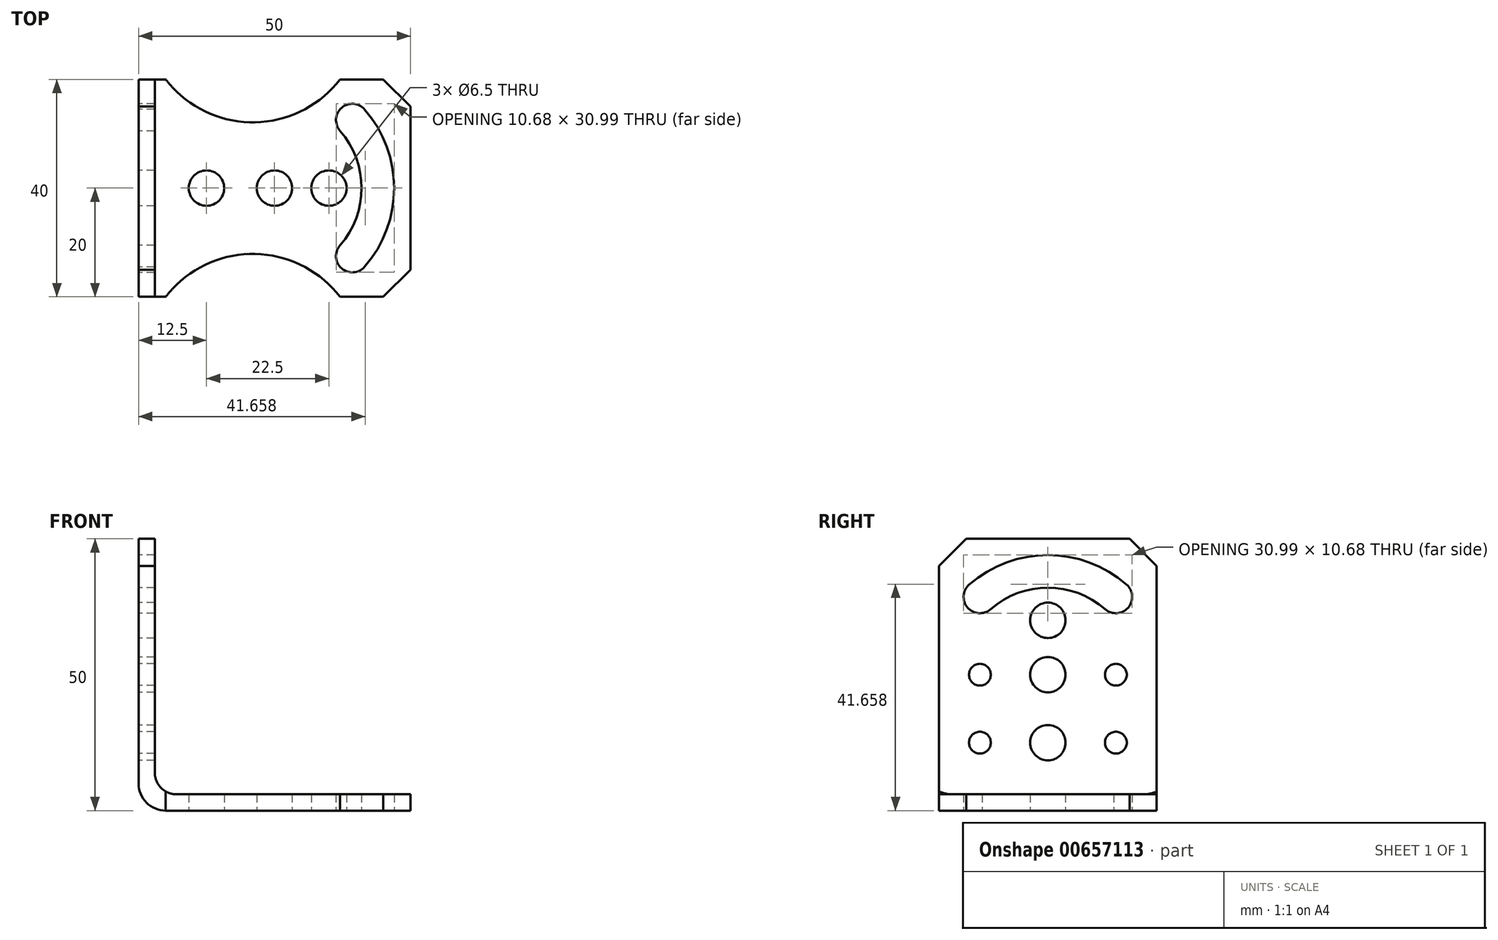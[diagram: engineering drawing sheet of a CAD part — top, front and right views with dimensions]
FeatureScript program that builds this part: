
annotation { "Feature Type Name" : "Feature", "Feature Type Description" : "" }
export const myFeature = defineFeature(function(context is Context, id is Id, definition is map)
    precondition{}
    {
        {
            var Q0;
            Q0=qCreatedBy(makeId("Front.planeOp"),FACE);
            var sketch = newSketch(context, id + "F0", { "sketchPlane" : qUnion([Q0])});
            skLineSegment(sketch, "E0", {"start": v(0, 0) * mm, "end": v(50, 0) * mm});
            skLineSegment(sketch, "E1", {"start": v(50, 0) * mm, "end": v(50, 5) * mm});
            skLineSegment(sketch, "E2", {"start": v(50, 5) * mm, "end": v(5, 5) * mm});
            skLineSegment(sketch, "E3", {"start": v(5, 5) * mm, "end": v(5, 50) * mm});
            skLineSegment(sketch, "E4", {"start": v(5, 50) * mm, "end": v(0, 50) * mm});
            skLineSegment(sketch, "E5", {"start": v(0, 50) * mm, "end": v(0, 0) * mm});
            skSolve(sketch);
        }
        {
            var Q0;
            Q0=qSketchRegion(id+"F0",true);
            extrude(context, id + "F1", {"entities" : qUnion([Q0]), "depth" : 40 * mm, "offsetDistance" : 25 * mm});
        }
        {
            var Q0;
            Q0=makeQuery(id+"F1.opExtrude","SWEPT_FACE",FACE,{"disambiguationData":[OSD([sQuery(id+"F0.wireOp",EDGE,"E0")])]});
            var sketch = newSketch(context, id + "F2", { "sketchPlane" : qUnion([Q0])});
            skCircle(sketch, "E6", {"center": v(25, 20) * mm, "radius": 3.25 * mm});
            skPoint(sketch, "E6.centerSnap0", {"position": v(0, 20) * mm});
            skArc(sketch, "E7", {"start": v(37.05, 9.47) * mm, "mid": v(37.34, 5.24) * mm, "end": v(41.57, 5.53) * mm});
            skArc(sketch, "E8", {"start": v(41.57, 34.47) * mm, "mid": v(37.34, 34.76) * mm, "end": v(37.05, 30.53) * mm});
            skArc(sketch, "E9", {"start": v(37.05, 9.47) * mm, "mid": v(41, 20) * mm, "end": v(37.05, 30.53) * mm});
            skArc(sketch, "E10", {"start": v(41.57, 5.53) * mm, "mid": v(47, 20) * mm, "end": v(41.57, 34.47) * mm});
            skCircle(sketch, "E11", {"center": v(12.5, 20) * mm, "radius": 3.25 * mm});
            skCircle(sketch, "E12", {"center": v(35, 20) * mm, "radius": 3.25 * mm});
            skPoint(sketch, "E12.centerSnap0", {"position": v(41, 20) * mm});
            skArc(sketch, "E13", {"start": v(37.05, 0) * mm, "mid": v(21.02, 7.9) * mm, "end": v(5, 0) * mm});
            skArc(sketch, "E14", {"start": v(5, 40) * mm, "mid": v(21.02, 32.1) * mm, "end": v(37.05, 40) * mm});
            skLineSegment(sketch, "E15", {"start": v(37.05, 0) * mm, "end": v(26.55, -9.52) * mm});
            skLineSegment(sketch, "E16", {"start": v(26.55, -9.52) * mm, "end": v(5, 0) * mm});
            skLineSegment(sketch, "E17", {"start": v(5, 40) * mm, "end": v(21.02, 52.32) * mm});
            skLineSegment(sketch, "E18", {"start": v(37.05, 40) * mm, "end": v(21.02, 52.32) * mm});
            skSolve(sketch);
        }
        {
            var Q0;
            Q0=qSketchRegion(id+"F2",true);
            extrude(context, id + "F3", {"entities" : qUnion([Q0]), "operationType" : NewBodyOperationType.REMOVE, "oppositeDirection" : true, "depth" : 25 * mm, "offsetDistance" : 25 * mm});
        }
        {
            var Q0;
            Q0=makeQuery(id+"F1.opExtrude","SWEPT_FACE",FACE,{"disambiguationData":[OSD([sQuery(id+"F0.wireOp",EDGE,"E5")])]});
            var sketch = newSketch(context, id + "F4", { "sketchPlane" : qUnion([Q0])});
            skCircle(sketch, "E19", {"center": v(20, 12.5) * mm, "radius": 3.25 * mm});
            skPoint(sketch, "E19.centerSnap0", {"position": v(20, 0) * mm});
            skCircle(sketch, "E20", {"center": v(20, 25) * mm, "radius": 3.25 * mm});
            skCircle(sketch, "E21", {"center": v(20, 35) * mm, "radius": 3.25 * mm});
            skArc(sketch, "E22", {"start": v(30.53, 37.05) * mm, "mid": v(20, 41) * mm, "end": v(9.47, 37.05) * mm});
            skArc(sketch, "E23", {"start": v(5.53, 41.57) * mm, "mid": v(5.24, 37.34) * mm, "end": v(9.47, 37.05) * mm});
            skArc(sketch, "E24", {"start": v(30.53, 37.05) * mm, "mid": v(34.76, 37.34) * mm, "end": v(34.47, 41.57) * mm});
            skArc(sketch, "E25", {"start": v(34.47, 41.57) * mm, "mid": v(20, 47) * mm, "end": v(5.53, 41.57) * mm});
            skCircle(sketch, "E26", {"center": v(32.5, 12.5) * mm, "radius": 2 * mm});
            skCircle(sketch, "E27", {"center": v(32.5, 25) * mm, "radius": 2 * mm});
            skCircle(sketch, "E28", {"center": v(7.5, 25) * mm, "radius": 2 * mm});
            skCircle(sketch, "E29", {"center": v(7.5, 12.5) * mm, "radius": 2 * mm});
            skSolve(sketch);
        }
        {
            var Q0;
            Q0=qSketchRegion(id+"F4",true);
            extrude(context, id + "F5", {"entities" : qUnion([Q0]), "operationType" : NewBodyOperationType.REMOVE, "oppositeDirection" : true, "depth" : 25 * mm, "offsetDistance" : 25 * mm});
        }
        {
            var Q0;
            Q0=makeQuery(id+"F1.opExtrude","CAP_EDGE",EDGE,{"disambiguationData":[OSD([sQuery(id+"F0.wireOp",EDGE,"E1")])],"isStart":false});
            chamfer(context, id + "F6", {"entities" : qUnion([Q0]), "width" : 5 * mm, "tangentPropagation" : true});
        }
        {
            var Q0;
            Q0=makeQuery(id+"F1.opExtrude","CAP_EDGE",EDGE,{"disambiguationData":[OSD([sQuery(id+"F0.wireOp",EDGE,"E1")])],"isStart":true});
            chamfer(context, id + "F7", {"entities" : qUnion([Q0]), "width" : 5 * mm, "tangentPropagation" : true});
        }
        {
            var Q0;
            Q0=qSketchRegion(id+"F2",true);
            extrude(context, id + "F8", {"entities" : qUnion([Q0]), "operationType" : NewBodyOperationType.REMOVE, "depth" : 25 * mm, "offsetDistance" : 25 * mm});
        }
        {
            var Q0;
            {var subQ0=sQuery(id+"F0.wireOp",EDGE,"E4");var subQ1=sQuery(id+"F0.wireOp",EDGE,"E2");var subQ2=sQuery(id+"F0.wireOp",EDGE,"E3");var subQ3=sQuery(id+"F0.wireOp",EDGE,"E0");var subQ4=sQuery(id+"F0.wireOp",EDGE,"E5");Q0=makeQuery(id+"F3.boolean.opBoolean","SPLIT",FACE,{"disambiguationData":[TD([makeQuery(id+"F1.opExtrude","SWEPT_FACE",FACE,{"disambiguationData":[OSD([subQ2])]})])],"derivedFrom":makeQuery(id+"F1.opExtrude","CAP_FACE",FACE,{"disambiguationData":[OSD([subQ3,sQuery(id+"F0.wireOp",EDGE,"E1"),subQ1,subQ2,subQ0,subQ4])],"isStart":false})});}
            var sketch = newSketch(context, id + "F9", { "sketchPlane" : qUnion([Q0])});
            skLineSegment(sketch, "E30.bottom", {"start": v(3, 3) * mm, "end": v(53.79, 3) * mm});
            skLineSegment(sketch, "E30.top", {"start": v(3, 60.6) * mm, "end": v(53.79, 60.6) * mm});
            skLineSegment(sketch, "E30.left", {"start": v(3, 3) * mm, "end": v(3, 60.6) * mm});
            skLineSegment(sketch, "E30.right", {"start": v(53.79, 3) * mm, "end": v(53.79, 60.6) * mm});
            skSolve(sketch);
        }
        {
            var Q0;
            Q0=qSketchRegion(id+"F9",true);
            extrude(context, id + "F10", {"entities" : qUnion([Q0]), "operationType" : NewBodyOperationType.REMOVE, "oppositeDirection" : true, "depth" : 51.1 * mm, "offsetDistance" : 25 * mm});
        }
        {
            var Q0;
            Q0=makeQuery(id+"F1.opExtrude","CAP_EDGE",EDGE,{"disambiguationData":[OSD([sQuery(id+"F0.wireOp",EDGE,"E4")])],"isStart":true});
            chamfer(context, id + "F11", {"entities" : qUnion([Q0]), "width" : 5 * mm, "tangentPropagation" : true});
        }
        {
            var Q0;
            Q0=makeQuery(id+"F1.opExtrude","CAP_EDGE",EDGE,{"disambiguationData":[OSD([sQuery(id+"F0.wireOp",EDGE,"E4")])],"isStart":false});
            chamfer(context, id + "F12", {"entities" : qUnion([Q0]), "width" : 5 * mm, "tangentPropagation" : true});
        }
        {
            var Q0;
            Q0=makeQuery(id+"F10.boolean.opBoolean","COPY",EDGE,{"derivedFrom":makeQuery(id+"F10.opExtrude","SWEPT_EDGE",EDGE,{"disambiguationData":[OSD([sQuery(id+"F9.wireOp",EDGE,"E30.bottom"),sQuery(id+"F9.wireOp",EDGE,"E30.left")])]})});
            fillet(context, id + "F13", {"entities" : qUnion([Q0]), "radius" : 4 * mm, "tangentPropagation" : true, "allowEdgeOverflow" : false});
        }
        {
            var Q0;
            Q0=makeQuery(id+"F1.opExtrude","SWEPT_EDGE",EDGE,{"disambiguationData":[OSD([sQuery(id+"F0.wireOp",EDGE,"E0"),sQuery(id+"F0.wireOp",EDGE,"E5")])]});
            fillet(context, id + "F14", {"entities" : qUnion([Q0]), "radius" : 5 * mm, "tangentPropagation" : true, "allowEdgeOverflow" : false});
        }
    });
